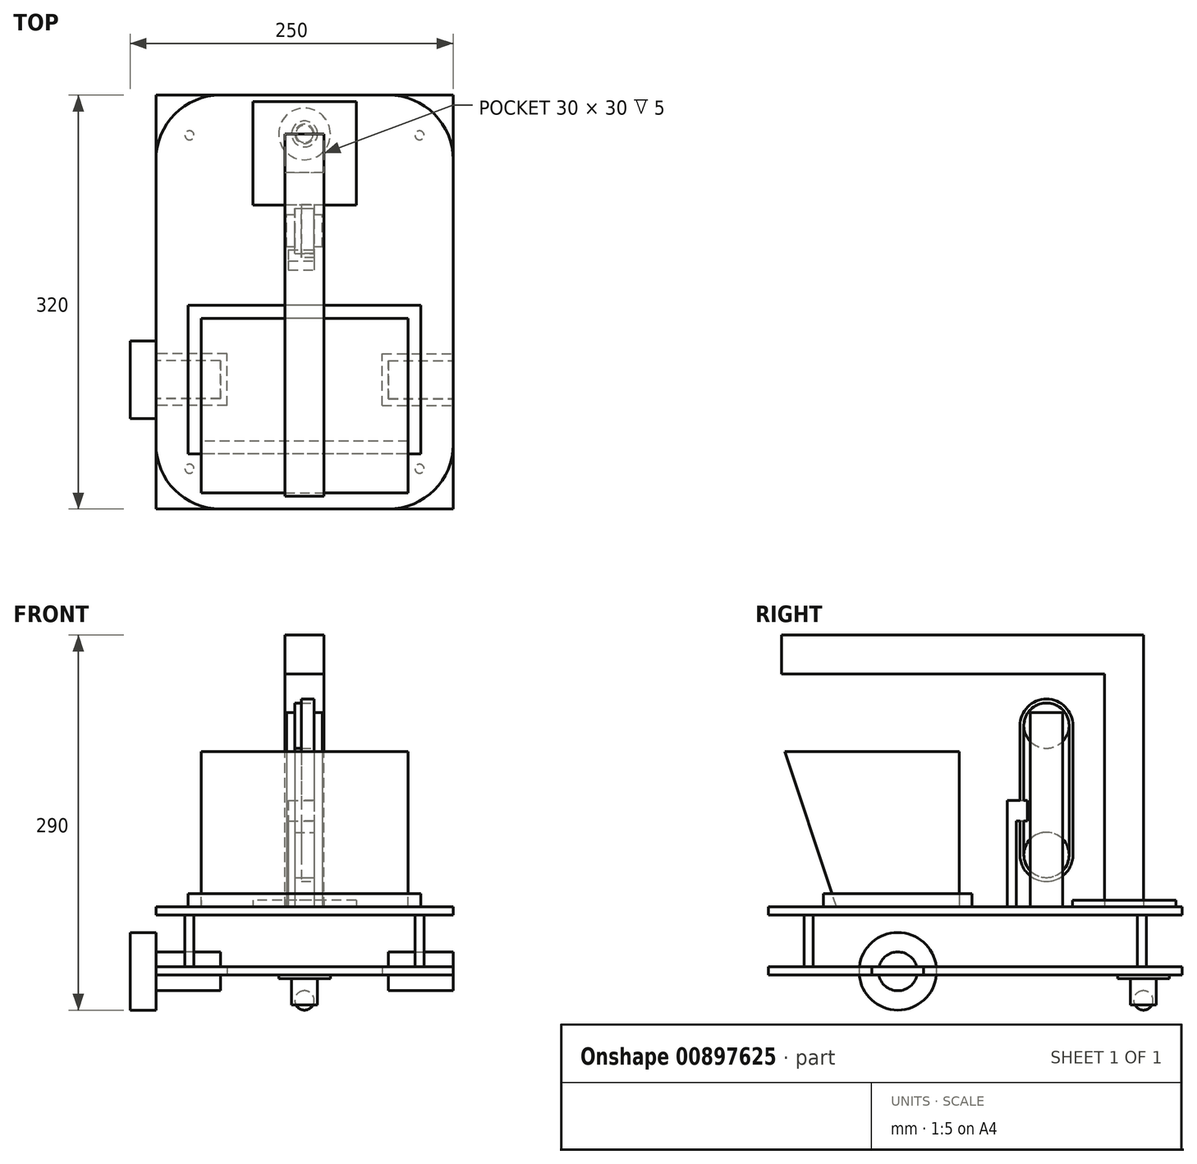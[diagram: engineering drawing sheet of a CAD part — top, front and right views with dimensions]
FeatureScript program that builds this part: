
annotation { "Feature Type Name" : "Feature", "Feature Type Description" : "" }
export const myFeature = defineFeature(function(context is Context, id is Id, definition is map)
    precondition{}
    {
        {
            var Q0;
            Q0=qCreatedBy(makeId("Top.planeOp"),FACE);
            var sketch = newSketch(context, id + "F0", { "sketchPlane" : qUnion([Q0])});
            skLineSegment(sketch, "E0.bottom", {"start": v(0, 0) * mm, "end": v(230, 0) * mm});
            skLineSegment(sketch, "E0.top", {"start": v(0, 320) * mm, "end": v(230, 320) * mm});
            skLineSegment(sketch, "E0.left", {"start": v(0, 0) * mm, "end": v(0, 320) * mm});
            skLineSegment(sketch, "E0.right", {"start": v(230, 0) * mm, "end": v(230, 320) * mm});
            skLineSegment(sketch, "E1.bottom", {"start": v(-20, 130) * mm, "end": v(0, 130) * mm});
            skLineSegment(sketch, "E1.top", {"start": v(-20, 70) * mm, "end": v(0, 70) * mm});
            skLineSegment(sketch, "E1.left", {"start": v(-20, 130) * mm, "end": v(-20, 70) * mm});
            skLineSegment(sketch, "E1.right", {"start": v(0, 130) * mm, "end": v(0, 70) * mm});
            skLineSegment(sketch, "E2.bottom", {"start": v(230, 130) * mm, "end": v(250, 130) * mm});
            skLineSegment(sketch, "E2.top", {"start": v(230, 70) * mm, "end": v(250, 70) * mm});
            skLineSegment(sketch, "E2.left", {"start": v(230, 130) * mm, "end": v(230, 70) * mm});
            skLineSegment(sketch, "E2.right", {"start": v(250, 130) * mm, "end": v(250, 70) * mm});
            skLineSegment(sketch, "E3", {"start": v(-20, 100) * mm, "end": v(250, 100) * mm, "construction": true});
            skSolve(sketch);
        }
        {
            var Q0;
            Q0=qCreatedBy(makeId("Right.planeOp"),FACE);
            var sketch = newSketch(context, id + "F1", { "sketchPlane" : qUnion([Q0])});
            skLineSegment(sketch, "E4.bottom", {"start": v(0, 0) * mm, "end": v(320, 0) * mm});
            skLineSegment(sketch, "E4.top", {"start": v(0, -6.35) * mm, "end": v(320, -6.35) * mm});
            skLineSegment(sketch, "E4.left", {"start": v(0, 0) * mm, "end": v(0, -6.35) * mm});
            skLineSegment(sketch, "E4.right", {"start": v(320, 0) * mm, "end": v(320, -6.35) * mm});
            skLineSegment(sketch, "E5", {"start": v(160, 0) * mm, "end": v(160, -52.7) * mm, "construction": true});
            skLineSegment(sketch, "E6.bottom", {"start": v(0, -52.7) * mm, "end": v(320, -52.7) * mm});
            skLineSegment(sketch, "E6.top", {"start": v(0, -46.35) * mm, "end": v(320, -46.35) * mm});
            skLineSegment(sketch, "E6.left", {"start": v(0, -52.7) * mm, "end": v(0, -46.35) * mm});
            skLineSegment(sketch, "E6.right", {"start": v(320, -52.7) * mm, "end": v(320, -46.35) * mm});
            skPoint(sketch, "E7.0", {"position": v(100, 0) * mm});
            skLineSegment(sketch, "E8", {"start": v(100, 0) * mm, "end": v(100, -50) * mm, "construction": true});
            skPoint(sketch, "E9.0", {"position": v(70, 0) * mm});
            skPoint(sketch, "E10.0", {"position": v(130, 0) * mm});
            skLineSegment(sketch, "E11", {"start": v(70, 0) * mm, "end": v(70, -50) * mm, "construction": true});
            skLineSegment(sketch, "E12", {"start": v(70, -50) * mm, "end": v(100, -50) * mm, "construction": true});
            skCircle(sketch, "E13", {"center": v(100, -50) * mm, "radius": 30 * mm});
            skLineSegment(sketch, "E14", {"start": v(100, -50) * mm, "end": v(100, -80) * mm, "construction": true});
            skSolve(sketch);
        }
        {
            var Q0;
            {var subQ3=sQuery(id+"F0.wireOp",EDGE,"E0.bottom");Q0=makeQuery(id+"F0.imprint","IMPRINT",FACE,{"disambiguationData":[TD([[makeQuery(id+"F0.imprint","IMPRINT",EDGE,{"derivedFrom":subQ3}),1.0]])]});}
            var Q1;
            Q1=sQuery(id+"F1.wireOp",VERTEX,"E4.top.end");
            extrude(context, id + "F2", {"entities" : qUnion([Q0]), "endBound" : BoundingType.UP_TO_VERTEX, "oppositeDirection" : true, "depth" : 25 * mm, "endBoundEntityVertex" : qUnion([Q1]), "offsetDistance" : 25 * mm});
        }
        {
            var Q0;
            {var subQ3=sQuery(id+"F0.wireOp",EDGE,"E0.bottom");Q0=makeQuery(id+"F0.imprint","IMPRINT",FACE,{"disambiguationData":[TD([[makeQuery(id+"F0.imprint","IMPRINT",EDGE,{"derivedFrom":subQ3}),1.0]])]});}
            var Q1;
            Q1=sQuery(id+"F1.wireOp",VERTEX,"E6.bottom.start");
            var Q2;
            Q2=sQuery(id+"F1.wireOp",VERTEX,"E6.top.start");
            extrude(context, id + "F3", {"entities" : qUnion([Q0]), "endBound" : BoundingType.UP_TO_VERTEX, "oppositeDirection" : true, "depth" : 25 * mm, "endBoundEntityVertex" : qUnion([Q1]), "offsetDistance" : 25 * mm, "hasSecondDirection" : true, "secondDirectionBound" : BoundingType.UP_TO_VERTEX, "secondDirectionOppositeDirection" : true, "secondDirectionDepth" : 25 * mm, "secondDirectionBoundEntityVertex" : qUnion([Q2])});
        }
        {
            var Q0;
            Q0=makeQuery(id+"F2.opExtrude","SWEPT_EDGE",EDGE,{"disambiguationData":[OSD([sQuery(id+"F0.wireOp",EDGE,"E0.bottom"),sQuery(id+"F0.wireOp",EDGE,"E0.right")])]});
            var Q1;
            Q1=makeQuery(id+"F2.opExtrude","SWEPT_EDGE",EDGE,{"disambiguationData":[OSD([sQuery(id+"F0.wireOp",EDGE,"E0.top"),sQuery(id+"F0.wireOp",EDGE,"E0.right")])]});
            var Q2;
            Q2=makeQuery(id+"F2.opExtrude","SWEPT_EDGE",EDGE,{"disambiguationData":[OSD([sQuery(id+"F0.wireOp",EDGE,"E0.top"),sQuery(id+"F0.wireOp",EDGE,"E0.left")])]});
            var Q3;
            Q3=makeQuery(id+"F2.opExtrude","SWEPT_EDGE",EDGE,{"disambiguationData":[OSD([sQuery(id+"F0.wireOp",EDGE,"E0.bottom"),sQuery(id+"F0.wireOp",EDGE,"E0.left")])]});
            var Q4;
            {var subQ0=sQuery(id+"F0.wireOp",EDGE,"E2.left");var subQ1=sQuery(id+"F0.wireOp",EDGE,"E0.right");var subQ2=sQuery(id+"F0.wireOp",EDGE,"E0.bottom");Q4=makeQuery(id+"F3.opExtrude","TWEAK_EDGE",EDGE,{"derivedFrom":[makeQuery(id+"F0.imprint","IMPRINT",EDGE,{"derivedFrom":subQ2}),makeQuery(id+"F0.imprint","IMPRINT",EDGE,{"disambiguationData":[TD([[makeQuery(id+"F0.imprint","INTERSECT",VERTEX,{"derivedFrom":[subQ2,subQ1]}),-1.0]])],"derivedFrom":subQ1}),makeQuery(id+"F0.imprint","IMPRINT",EDGE,{"disambiguationData":[TD([[makeQuery(id+"F0.imprint","INTERSECT",VERTEX,{"derivedFrom":[sQuery(id+"F0.wireOp",EDGE,"E0.top"),subQ1]}),1.0]])],"derivedFrom":subQ1}),makeQuery(id+"F0.imprint","IMPRINT",EDGE,{"derivedFrom":subQ0})]});}
            var Q5;
            {var subQ0=sQuery(id+"F0.wireOp",EDGE,"E2.left");var subQ1=sQuery(id+"F0.wireOp",EDGE,"E0.right");var subQ2=sQuery(id+"F0.wireOp",EDGE,"E0.top");Q5=makeQuery(id+"F3.opExtrude","TWEAK_EDGE",EDGE,{"derivedFrom":[makeQuery(id+"F0.imprint","IMPRINT",EDGE,{"derivedFrom":subQ2}),makeQuery(id+"F0.imprint","IMPRINT",EDGE,{"disambiguationData":[TD([[makeQuery(id+"F0.imprint","INTERSECT",VERTEX,{"derivedFrom":[sQuery(id+"F0.wireOp",EDGE,"E0.bottom"),subQ1]}),-1.0]])],"derivedFrom":subQ1}),makeQuery(id+"F0.imprint","IMPRINT",EDGE,{"disambiguationData":[TD([[makeQuery(id+"F0.imprint","INTERSECT",VERTEX,{"derivedFrom":[subQ2,subQ1]}),1.0]])],"derivedFrom":subQ1}),makeQuery(id+"F0.imprint","IMPRINT",EDGE,{"derivedFrom":subQ0})]});}
            var Q6;
            {var subQ0=sQuery(id+"F0.wireOp",EDGE,"E1.right");var subQ1=sQuery(id+"F0.wireOp",EDGE,"E0.left");var subQ2=sQuery(id+"F0.wireOp",EDGE,"E0.top");Q6=makeQuery(id+"F3.opExtrude","TWEAK_EDGE",EDGE,{"derivedFrom":[makeQuery(id+"F0.imprint","IMPRINT",EDGE,{"derivedFrom":subQ2}),makeQuery(id+"F0.imprint","IMPRINT",EDGE,{"disambiguationData":[TD([[makeQuery(id+"F0.imprint","INTERSECT",VERTEX,{"derivedFrom":[sQuery(id+"F0.wireOp",EDGE,"E0.bottom"),subQ1]}),-1.0]])],"derivedFrom":subQ1}),makeQuery(id+"F0.imprint","IMPRINT",EDGE,{"disambiguationData":[TD([[makeQuery(id+"F0.imprint","INTERSECT",VERTEX,{"derivedFrom":[subQ2,subQ1]}),1.0]])],"derivedFrom":subQ1}),makeQuery(id+"F0.imprint","IMPRINT",EDGE,{"derivedFrom":subQ0})]});}
            var Q7;
            {var subQ0=sQuery(id+"F0.wireOp",EDGE,"E1.right");var subQ1=sQuery(id+"F0.wireOp",EDGE,"E0.left");var subQ2=sQuery(id+"F0.wireOp",EDGE,"E0.bottom");Q7=makeQuery(id+"F3.opExtrude","TWEAK_EDGE",EDGE,{"derivedFrom":[makeQuery(id+"F0.imprint","IMPRINT",EDGE,{"derivedFrom":subQ2}),makeQuery(id+"F0.imprint","IMPRINT",EDGE,{"disambiguationData":[TD([[makeQuery(id+"F0.imprint","INTERSECT",VERTEX,{"derivedFrom":[subQ2,subQ1]}),-1.0]])],"derivedFrom":subQ1}),makeQuery(id+"F0.imprint","IMPRINT",EDGE,{"disambiguationData":[TD([[makeQuery(id+"F0.imprint","INTERSECT",VERTEX,{"derivedFrom":[sQuery(id+"F0.wireOp",EDGE,"E0.top"),subQ1]}),1.0]])],"derivedFrom":subQ1}),makeQuery(id+"F0.imprint","IMPRINT",EDGE,{"derivedFrom":subQ0})]});}
            fillet(context, id + "F4", {"entities" : qUnion([Q0, Q1, Q2, Q3, Q4, Q5, Q6, Q7]), "radius" : 50 * mm, "tangentPropagation" : true, "allowEdgeOverflow" : false});
        }
        {
            var Q0;
            Q0=makeQuery(id+"F2.opExtrude","SWEPT_FACE",FACE,{"disambiguationData":[OSD([sQuery(id+"F0.wireOp",EDGE,"E0.left"),sQuery(id+"F0.wireOp",EDGE,"E1.right")])]});
            var Q1;
            Q1=makeQuery(id+"F2.opExtrude","SWEPT_FACE",FACE,{"disambiguationData":[OSD([sQuery(id+"F0.wireOp",EDGE,"E0.right"),sQuery(id+"F0.wireOp",EDGE,"E2.left")])]});
            cPlane(context, id + "F5", {"entities" : qUnion([Q0, Q1]), "cplaneType" : CPlaneType.MID_PLANE, "offset" : 25 * mm, "width" : 150 * mm, "height" : 150 * mm});
        }
        {
            var Q0;
            {var subQ0=sQuery(id+"F1.wireOp",EDGE,"E13");var subQ1=sQuery(id+"F1.wireOp",EDGE,"E6.bottom");var subQ2=makeQuery(id+"F1.imprint","INTERSECT",VERTEX,{"disambiguationData":[OD(0.0)],"derivedFrom":[subQ1,subQ0]});Q0=makeQuery(id+"F1.imprint","IMPRINT",FACE,{"disambiguationData":[TD([[makeQuery(id+"F1.imprint","IMPRINT",EDGE,{"disambiguationData":[TD([[subQ2,-1.0]])],"derivedFrom":subQ1}),1.0]])]});}
            var Q1;
            {var subQ0=sQuery(id+"F1.wireOp",EDGE,"E13");var subQ1=sQuery(id+"F1.wireOp",EDGE,"E6.bottom");var subQ2=makeQuery(id+"F1.imprint","INTERSECT",VERTEX,{"disambiguationData":[OD(0.0)],"derivedFrom":[subQ1,subQ0]});Q1=makeQuery(id+"F1.imprint","IMPRINT",FACE,{"disambiguationData":[TD([[makeQuery(id+"F1.imprint","IMPRINT",EDGE,{"disambiguationData":[TD([[subQ2,-1.0]])],"derivedFrom":subQ1}),-1.0]])]});}
            var Q2;
            {var subQ0=sQuery(id+"F1.wireOp",EDGE,"E13");var subQ1=sQuery(id+"F1.wireOp",EDGE,"E6.top");var subQ2=makeQuery(id+"F1.imprint","INTERSECT",VERTEX,{"disambiguationData":[OD(0.0)],"derivedFrom":[subQ1,subQ0]});Q2=makeQuery(id+"F1.imprint","IMPRINT",FACE,{"disambiguationData":[TD([[makeQuery(id+"F1.imprint","IMPRINT",EDGE,{"disambiguationData":[TD([[subQ2,-1.0]])],"derivedFrom":subQ1}),1.0]])]});}
            var Q3;
            Q3=sQuery(id+"F0.wireOp",VERTEX,"E3.start");
            extrude(context, id + "F6", {"entities" : qUnion([Q0, Q1, Q2]), "operationType" : NewBodyOperationType.ADD, "endBound" : BoundingType.UP_TO_VERTEX, "oppositeDirection" : true, "depth" : 25 * mm, "endBoundEntityVertex" : qUnion([Q3]), "offsetDistance" : 25 * mm});
        }
        {
            var Q0;
            Q0=makeQuery(id+"F6.opExtrude","CAP_FACE",FACE,{"disambiguationData":[OSD([sQuery(id+"F1.wireOp",EDGE,"E13")])],"isStart":true});
            var sketch = newSketch(context, id + "F7", { "sketchPlane" : qUnion([Q0])});
            skPoint(sketch, "E15.0", {"position": v(100, -50) * mm});
            skCircle(sketch, "E16", {"center": v(100, -50) * mm, "radius": 15 * mm});
            skSolve(sketch);
        }
        {
            var Q0;
            Q0 = qSketchRegion(id + "F7", true);
            extrude(context, id + "F8", {"entities" : qUnion([Q0]), "depth" : 50 * mm, "offsetDistance" : 25 * mm});
        }
        {
            var Q0;
            Q0=makeQuery(id+"F3.opExtrude","CAP_FACE",FACE,{"disambiguationData":[OSD([sQuery(id+"F0.wireOp",EDGE,"E0.bottom"),sQuery(id+"F0.wireOp",EDGE,"E0.top"),sQuery(id+"F0.wireOp",EDGE,"E0.left"),sQuery(id+"F0.wireOp",EDGE,"E0.right"),sQuery(id+"F0.wireOp",EDGE,"E1.right"),sQuery(id+"F0.wireOp",EDGE,"E2.left")])],"isStart":true});
            var sketch = newSketch(context, id + "F9", { "sketchPlane" : qUnion([Q0])});
            skLineSegment(sketch, "E17.0", {"start": v(0, 50) * mm, "end": v(0, 270) * mm, "construction": true});
            skArc(sketch, "E17.1", {"start": v(50, 320) * mm, "mid": v(14.64, 305.36) * mm, "end": v(0, 270) * mm, "construction": true});
            skLineSegment(sketch, "E17.2", {"start": v(50, 320) * mm, "end": v(180, 320) * mm, "construction": true});
            skArc(sketch, "E17.3", {"start": v(230, 270) * mm, "mid": v(215.36, 305.36) * mm, "end": v(180, 320) * mm, "construction": true});
            skLineSegment(sketch, "E17.4", {"start": v(230, 270) * mm, "end": v(230, 50) * mm, "construction": true});
            skArc(sketch, "E17.5", {"start": v(180, 0) * mm, "mid": v(215.36, 14.64) * mm, "end": v(230, 50) * mm, "construction": true});
            skLineSegment(sketch, "E17.6", {"start": v(50, 0) * mm, "end": v(180, 0) * mm, "construction": true});
            skArc(sketch, "E17.7", {"start": v(0, 50) * mm, "mid": v(14.64, 14.64) * mm, "end": v(50, 0) * mm, "construction": true});
            skLineSegment(sketch, "E18", {"start": v(14.64, 305.36) * mm, "end": v(215.36, 14.64) * mm, "construction": true});
            skLineSegment(sketch, "E19", {"start": v(215.36, 305.36) * mm, "end": v(14.64, 14.64) * mm, "construction": true});
            skLineSegment(sketch, "E20", {"start": v(115, 320) * mm, "end": v(115, 0) * mm, "construction": true});
            skCircle(sketch, "E21", {"center": v(26, 288.9) * mm, "radius": 3.5 * mm});
            skCircle(sketch, "E22", {"center": v(26, 31.1) * mm, "radius": 3.5 * mm});
            skLineSegment(sketch, "E23", {"start": v(14.64, 305.36) * mm, "end": v(26, 288.9) * mm, "construction": true});
            skLineSegment(sketch, "E24", {"start": v(26, 31.1) * mm, "end": v(14.64, 14.64) * mm, "construction": true});
            skSolve(sketch);
        }
        {
            var Q0;
            Q0=makeQuery(id+"F9.imprint","IMPRINT",FACE,{"disambiguationData":[TD([[makeQuery(id+"F9.imprint","IMPRINT",EDGE,{"derivedFrom":sQuery(id+"F9.wireOp",EDGE,"E21")}),1.0]])]});
            var Q1;
            Q1=makeQuery(id+"F9.imprint","IMPRINT",FACE,{"disambiguationData":[TD([[makeQuery(id+"F9.imprint","IMPRINT",EDGE,{"derivedFrom":sQuery(id+"F9.wireOp",EDGE,"E22")}),1.0]])]});
            var Q2;
            Q2=makeQuery(id+"F2.opExtrude","CAP_FACE",FACE,{"disambiguationData":[OSD([sQuery(id+"F0.wireOp",EDGE,"E0.bottom"),sQuery(id+"F0.wireOp",EDGE,"E0.top"),sQuery(id+"F0.wireOp",EDGE,"E0.left"),sQuery(id+"F0.wireOp",EDGE,"E0.right"),sQuery(id+"F0.wireOp",EDGE,"E1.right"),sQuery(id+"F0.wireOp",EDGE,"E2.left")])],"isStart":false});
            extrude(context, id + "F10", {"entities" : qUnion([Q0, Q1]), "endBound" : BoundingType.UP_TO_SURFACE, "depth" : 25 * mm, "endBoundEntityFace" : qUnion([Q2]), "offsetDistance" : 25 * mm});
        }
        {
            var Q0;
            Q0=makeQuery(id+"F2.opExtrude","CAP_FACE",FACE,{"disambiguationData":[OSD([sQuery(id+"F0.wireOp",EDGE,"E0.bottom"),sQuery(id+"F0.wireOp",EDGE,"E0.top"),sQuery(id+"F0.wireOp",EDGE,"E0.left"),sQuery(id+"F0.wireOp",EDGE,"E0.right"),sQuery(id+"F0.wireOp",EDGE,"E1.right"),sQuery(id+"F0.wireOp",EDGE,"E2.left")])],"isStart":true});
            var sketch = newSketch(context, id + "F11", { "sketchPlane" : qUnion([Q0])});
            skLineSegment(sketch, "E25", {"start": v(115, 320) * mm, "end": v(115, 0) * mm, "construction": true});
            skLineSegment(sketch, "E26.bottom", {"start": v(195, 147.5) * mm, "end": v(35, 147.5) * mm});
            skLineSegment(sketch, "E26.top", {"start": v(195, 52.5) * mm, "end": v(35, 52.5) * mm});
            skLineSegment(sketch, "E26.left", {"start": v(195, 147.5) * mm, "end": v(195, 52.5) * mm});
            skLineSegment(sketch, "E26.right", {"start": v(35, 147.5) * mm, "end": v(35, 52.5) * mm});
            skPoint(sketch, "E26.middle", {"position": v(115, 100) * mm});
            skLineSegment(sketch, "E27.bottom", {"start": v(155, 315) * mm, "end": v(75, 315) * mm});
            skLineSegment(sketch, "E27.top", {"start": v(155, 235) * mm, "end": v(75, 235) * mm});
            skLineSegment(sketch, "E27.left", {"start": v(155, 315) * mm, "end": v(155, 235) * mm});
            skLineSegment(sketch, "E27.right", {"start": v(75, 315) * mm, "end": v(75, 235) * mm});
            skPoint(sketch, "E27.middle", {"position": v(115, 275) * mm});
            skLineSegment(sketch, "E28.bottom", {"start": v(130, 290) * mm, "end": v(100, 290) * mm});
            skLineSegment(sketch, "E28.top", {"start": v(130, 260) * mm, "end": v(100, 260) * mm});
            skLineSegment(sketch, "E28.left", {"start": v(130, 290) * mm, "end": v(130, 260) * mm});
            skLineSegment(sketch, "E28.right", {"start": v(100, 290) * mm, "end": v(100, 260) * mm});
            skLineSegment(sketch, "E29.0", {"start": v(205, 157.5) * mm, "end": v(25, 157.5) * mm});
            skLineSegment(sketch, "E29.1", {"start": v(205, 157.5) * mm, "end": v(205, 42.5) * mm});
            skLineSegment(sketch, "E29.2", {"start": v(205, 42.5) * mm, "end": v(25, 42.5) * mm});
            skLineSegment(sketch, "E29.3", {"start": v(25, 157.5) * mm, "end": v(25, 42.5) * mm});
            skPoint(sketch, "E30.middle", {"position": v(115, 215) * mm});
            skLineSegment(sketch, "E31", {"start": v(125.67, 215) * mm, "end": v(104.32, 215) * mm, "construction": true});
            skLineSegment(sketch, "E32.bottom", {"start": v(128.85, 202.5) * mm, "end": v(122.5, 202.5) * mm});
            skLineSegment(sketch, "E32.top", {"start": v(128.85, 227.5) * mm, "end": v(122.5, 227.5) * mm});
            skLineSegment(sketch, "E32.left", {"start": v(128.85, 202.5) * mm, "end": v(128.85, 227.5) * mm});
            skLineSegment(sketch, "E32.right", {"start": v(122.5, 202.5) * mm, "end": v(122.5, 227.5) * mm});
            skPoint(sketch, "E32.middle", {"position": v(125.67, 215) * mm});
            skLineSegment(sketch, "E33.bottom", {"start": v(107.5, 202.5) * mm, "end": v(101.15, 202.5) * mm});
            skLineSegment(sketch, "E33.top", {"start": v(107.5, 227.5) * mm, "end": v(101.15, 227.5) * mm});
            skLineSegment(sketch, "E33.left", {"start": v(107.5, 202.5) * mm, "end": v(107.5, 227.5) * mm});
            skLineSegment(sketch, "E33.right", {"start": v(101.15, 202.5) * mm, "end": v(101.15, 227.5) * mm});
            skPoint(sketch, "E33.middle", {"position": v(104.32, 215) * mm});
            skPoint(sketch, "E34", {"position": v(115, 157.5) * mm});
            skSolve(sketch);
        }
        {
            var Q0;
            Q0=makeQuery(id+"F11.imprint","IMPRINT",FACE,{"disambiguationData":[TD([[makeQuery(id+"F11.imprint","IMPRINT",EDGE,{"derivedFrom":sQuery(id+"F11.wireOp",EDGE,"E26.bottom")}),1.0]])]});
            extrude(context, id + "F12", {"entities" : qUnion([Q0]), "operationType" : NewBodyOperationType.ADD, "depth" : 120 * mm, "offsetDistance" : 25 * mm});
        }
        {
            var Q0;
            Q0=makeQuery(id+"F11.imprint","IMPRINT",FACE,{"disambiguationData":[TD([[makeQuery(id+"F11.imprint","IMPRINT",EDGE,{"derivedFrom":sQuery(id+"F11.wireOp",EDGE,"E27.bottom")}),1.0]])]});
            extrude(context, id + "F13", {"entities" : qUnion([Q0]), "operationType" : NewBodyOperationType.ADD, "depth" : 5 * mm, "offsetDistance" : 25 * mm});
        }
        {
            var Q0;
            Q0=makeQuery(id+"F12.opExtrude","SWEPT_FACE",FACE,{"disambiguationData":[OSD([sQuery(id+"F11.wireOp",EDGE,"E26.left")])]});
            var sketch = newSketch(context, id + "F14", { "sketchPlane" : qUnion([Q0])});
            skLineSegment(sketch, "E35", {"start": v(52.5, 0) * mm, "end": v(12.5, 120) * mm});
            skLineSegment(sketch, "E36", {"start": v(12.5, 120) * mm, "end": v(52.5, 120) * mm});
            skLineSegment(sketch, "E37.0", {"start": v(52.5, 120) * mm, "end": v(52.5, 0) * mm});
            skSolve(sketch);
        }
        {
            var Q0;
            Q0=makeQuery(id+"F14.imprint","IMPRINT",FACE,{"disambiguationData":[TD([[makeQuery(id+"F14.imprint","IMPRINT",EDGE,{"derivedFrom":sQuery(id+"F14.wireOp",EDGE,"E35")}),-1.0]])]});
            var Q1;
            Q1=makeQuery(id+"F12.opExtrude","SWEPT_FACE",FACE,{"disambiguationData":[OSD([sQuery(id+"F11.wireOp",EDGE,"E26.right")])]});
            var Q2;
            Q2=makeQuery(id+"F12.opExtrude","CAP_VERTEX",VERTEX,{"disambiguationData":[OSD([sQuery(id+"F11.wireOp",EDGE,"E26.top"),sQuery(id+"F11.wireOp",EDGE,"E26.right")])],"isStart":false});
            extrude(context, id + "F15", {"entities" : qUnion([Q0]), "operationType" : NewBodyOperationType.ADD, "endBound" : BoundingType.UP_TO_VERTEX, "oppositeDirection" : true, "depth" : 25 * mm, "endBoundEntityFace" : qUnion([Q1]), "endBoundEntityVertex" : qUnion([Q2]), "offsetDistance" : 25 * mm});
        }
        {
            var Q0;
            Q0=makeQuery(id+"F12.opExtrude","CAP_FACE",FACE,{"disambiguationData":[OSD([sQuery(id+"F11.wireOp",EDGE,"E26.bottom"),sQuery(id+"F11.wireOp",EDGE,"E26.top"),sQuery(id+"F11.wireOp",EDGE,"E26.left"),sQuery(id+"F11.wireOp",EDGE,"E26.right")])],"isStart":false});
            shell(context, id + "F16", {"entities" : qUnion([Q0]), "thickness" : 0.05 * mm});
        }
        {
            var Q0;
            Q0=makeQuery(id+"F3.opExtrude","CAP_FACE",FACE,{"disambiguationData":[OSD([sQuery(id+"F0.wireOp",EDGE,"E0.bottom"),sQuery(id+"F0.wireOp",EDGE,"E0.top"),sQuery(id+"F0.wireOp",EDGE,"E0.left"),sQuery(id+"F0.wireOp",EDGE,"E0.right"),sQuery(id+"F0.wireOp",EDGE,"E1.right"),sQuery(id+"F0.wireOp",EDGE,"E2.left")])],"isStart":false});
            var sketch = newSketch(context, id + "F17", { "sketchPlane" : qUnion([Q0])});
            skLineSegment(sketch, "E38.0", {"start": v(0, -85) * mm, "end": v(0, -115) * mm});
            skLineSegment(sketch, "E39.0", {"start": v(50, -85) * mm, "end": v(50, -115) * mm, "construction": true});
            skLineSegment(sketch, "E40", {"start": v(50, -115) * mm, "end": v(0, -115) * mm, "construction": true});
            skLineSegment(sketch, "E41", {"start": v(50, -85) * mm, "end": v(0, -85) * mm, "construction": true});
            skLineSegment(sketch, "E42.0", {"start": v(55, -120) * mm, "end": v(0, -120) * mm});
            skLineSegment(sketch, "E42.1", {"start": v(55, -80) * mm, "end": v(55, -120) * mm});
            skLineSegment(sketch, "E42.2", {"start": v(55, -80) * mm, "end": v(0, -80) * mm});
            skLineSegment(sketch, "E43", {"start": v(115, -320) * mm, "end": v(115, -290) * mm, "construction": true});
            skCircle(sketch, "E44", {"center": v(115, -290) * mm, "radius": 20 * mm});
            skLineSegment(sketch, "E45.MirrorCS", {"start": v(175, -120) * mm, "end": v(230, -120) * mm});
            skLineSegment(sketch, "E46.MirrorCS", {"start": v(175, -80) * mm, "end": v(230, -80) * mm});
            skLineSegment(sketch, "E47.MirrorCS", {"start": v(175, -80) * mm, "end": v(175, -120) * mm});
            skSolve(sketch);
        }
        {
            var Q0;
            {var subQ1=sQuery(id+"F17.wireOp",EDGE,"E38.0");Q0=makeQuery(id+"F17.imprint","IMPRINT",FACE,{"disambiguationData":[TD([[makeQuery(id+"F17.imprint","IMPRINT",EDGE,{"derivedFrom":subQ1}),1.0]])]});}
            var Q1;
            {var subQ0=sQuery(id+"F17.wireOp",EDGE,"E45.MirrorCS");Q1=makeQuery(id+"F17.imprint","IMPRINT",FACE,{"disambiguationData":[TD([[makeQuery(id+"F17.imprint","IMPRINT",EDGE,{"derivedFrom":subQ0}),1.0]])]});}
            var Q2;
            Q2=makeQuery(id+"F3.opExtrude","CAP_FACE",FACE,{"disambiguationData":[OSD([sQuery(id+"F0.wireOp",EDGE,"E0.bottom"),sQuery(id+"F0.wireOp",EDGE,"E0.top"),sQuery(id+"F0.wireOp",EDGE,"E0.left"),sQuery(id+"F0.wireOp",EDGE,"E0.right"),sQuery(id+"F0.wireOp",EDGE,"E1.right"),sQuery(id+"F0.wireOp",EDGE,"E2.left")])],"isStart":true});
            extrude(context, id + "F18", {"entities" : qUnion([Q0, Q1]), "operationType" : NewBodyOperationType.REMOVE, "endBound" : BoundingType.UP_TO_SURFACE, "oppositeDirection" : true, "depth" : 25 * mm, "endBoundEntityFace" : qUnion([Q2]), "offsetDistance" : 25 * mm});
        }
        {
            var Q0;
            Q0=qCreatedBy(makeId("Front.planeOp"),FACE);
            var Q1;
            Q1=sQuery(id+"F17.wireOp",VERTEX,"E43.end");
            cPlane(context, id + "F19", {"entities" : qUnion([Q0, Q1]), "cplaneType" : CPlaneType.PLANE_POINT, "offset" : 25 * mm, "width" : 150 * mm, "height" : 150 * mm});
        }
        {
            var Q0;
            Q0=qCreatedBy(id+"F19.planeOp",FACE);
            var sketch = newSketch(context, id + "F20", { "sketchPlane" : qUnion([Q0])});
            skPoint(sketch, "E48.0", {"position": v(115, -52.7) * mm});
            skLineSegment(sketch, "E49.0", {"start": v(115, -52.7) * mm, "end": v(95, -52.7) * mm});
            skLineSegment(sketch, "E50", {"start": v(115, -52.7) * mm, "end": v(115, -76) * mm});
            skLineSegment(sketch, "E51", {"start": v(115, -76) * mm, "end": v(105, -76) * mm});
            skLineSegment(sketch, "E52", {"start": v(95, -55.7) * mm, "end": v(95, -52.7) * mm});
            skArc(sketch, "E53", {"start": v(115, -65) * mm, "mid": v(107.5, -72.5) * mm, "end": v(115, -80) * mm});
            skLineSegment(sketch, "E54", {"start": v(105, -76) * mm, "end": v(105, -55.7) * mm});
            skLineSegment(sketch, "E55", {"start": v(105, -55.7) * mm, "end": v(95, -55.7) * mm});
            skLineSegment(sketch, "E56", {"start": v(115, -80) * mm, "end": v(115, -76) * mm});
            skLineSegment(sketch, "E57.0", {"start": v(0, -20) * mm, "end": v(0, -80) * mm});
            skLineSegment(sketch, "E58", {"start": v(0, -80) * mm, "end": v(115, -80) * mm, "construction": true});
            skSolve(sketch);
        }
        {
            var Q0;
            {var subQ0=sQuery(id+"F20.wireOp",EDGE,"E56");Q0=makeQuery(id+"F20.imprint","IMPRINT",FACE,{"disambiguationData":[TD([[makeQuery(id+"F20.imprint","IMPRINT",EDGE,{"derivedFrom":subQ0}),1.0]])]});}
            var Q1;
            {var subQ5=sQuery(id+"F20.wireOp",EDGE,"E49.0");Q1=makeQuery(id+"F20.imprint","IMPRINT",FACE,{"disambiguationData":[TD([[makeQuery(id+"F20.imprint","IMPRINT",EDGE,{"derivedFrom":subQ5}),1.0]])]});}
            var Q2;
            Q2=sQuery(id+"F20.wireOp",EDGE,"E50");
            revolve(context, id + "F21", {"surfaceOperationType" : NewSurfaceOperationType.NEW, "entities" : qUnion([Q0, Q1]), "axis" : qUnion([Q2]), "revolveType" : RevolveType.FULL});
        }
        {
            var Q0;
            Q0=qCreatedBy(makeId("Right.planeOp"),FACE);
            var Q1;
            Q1=sQuery(id+"F11.wireOp",VERTEX,"E28.bottom.start");
            cPlane(context, id + "F22", {"entities" : qUnion([Q0, Q1]), "cplaneType" : CPlaneType.PLANE_POINT, "offset" : 25 * mm, "width" : 150 * mm, "height" : 150 * mm});
        }
        {
            var Q0;
            Q0=qCreatedBy(id+"F22.planeOp",FACE);
            var sketch = newSketch(context, id + "F23", { "sketchPlane" : qUnion([Q0])});
            skPoint(sketch, "E59.0", {"position": v(290, 0) * mm});
            skPoint(sketch, "E60.0", {"position": v(260, 0) * mm});
            skLineSegment(sketch, "E61.bottom", {"start": v(290, 0) * mm, "end": v(260, 0) * mm});
            skLineSegment(sketch, "E61.top", {"start": v(290, 210) * mm, "end": v(260, 210) * mm});
            skLineSegment(sketch, "E61.left", {"start": v(290, 0) * mm, "end": v(290, 210) * mm});
            skLineSegment(sketch, "E61.right", {"start": v(260, 0) * mm, "end": v(260, 180) * mm});
            skLineSegment(sketch, "E62.bottom", {"start": v(260, 210) * mm, "end": v(10, 210) * mm});
            skLineSegment(sketch, "E62.top", {"start": v(260, 180) * mm, "end": v(10, 180) * mm});
            skLineSegment(sketch, "E62.right", {"start": v(10, 210) * mm, "end": v(10, 180) * mm});
            skSolve(sketch);
        }
        {
            var Q0;
            Q0 = qSketchRegion(id + "F23", true);
            var Q1;
            Q1=sQuery(id+"F11.wireOp",VERTEX,"E28.top.end");
            extrude(context, id + "F24", {"entities" : qUnion([Q0]), "endBound" : BoundingType.UP_TO_VERTEX, "oppositeDirection" : true, "depth" : 25 * mm, "endBoundEntityVertex" : qUnion([Q1]), "offsetDistance" : 25 * mm});
        }
        {
            var Q0;
            Q0=makeQuery(id+"F6.opExtrude","SWEPT_BODY",BODY,{"disambiguationData":[OSD([sQuery(id+"F1.wireOp",EDGE,"E13")])]});
            var Q1;
            Q1=makeQuery(id+"F8.opExtrude","SWEPT_BODY",BODY,{"disambiguationData":[OSD([sQuery(id+"F7.wireOp",EDGE,"E16")])]});
            var Q2;
            Q2=makeQuery(id+"F10.opExtrude","SWEPT_BODY",BODY,{"disambiguationData":[OSD([sQuery(id+"F9.wireOp",EDGE,"E21")])]});
            var Q3;
            Q3=makeQuery(id+"F10.opExtrude","SWEPT_BODY",BODY,{"disambiguationData":[OSD([sQuery(id+"F9.wireOp",EDGE,"E22")])]});
            var Q4;
            Q4=qCreatedBy(id+"F5.planeOp",FACE);
            mirror(context, id + "F25", {"entities" : qUnion([Q0, Q1, Q2, Q3]), "mirrorPlane" : qUnion([Q4])});
        }
        {
            var Q0;
            Q0=makeQuery(id+"F11.imprint","IMPRINT",FACE,{"disambiguationData":[TD([[makeQuery(id+"F11.imprint","IMPRINT",EDGE,{"derivedFrom":sQuery(id+"F11.wireOp",EDGE,"E26.bottom")}),1.0]])]});
            var Q1;
            Q1=makeQuery(id+"F11.imprint","IMPRINT",FACE,{"disambiguationData":[TD([[makeQuery(id+"F11.imprint","IMPRINT",EDGE,{"derivedFrom":sQuery(id+"F11.wireOp",EDGE,"E26.bottom")}),-1.0]])]});
            extrude(context, id + "F26", {"entities" : qUnion([Q0, Q1]), "depth" : 10 * mm, "offsetDistance" : 25 * mm});
        }
        {
            var Q0;
            Q0=makeQuery(id+"F11.imprint","IMPRINT",FACE,{"disambiguationData":[TD([[makeQuery(id+"F11.imprint","IMPRINT",EDGE,{"derivedFrom":sQuery(id+"F11.wireOp",EDGE,"E32.bottom")}),-1.0]])]});
            var Q1;
            Q1=makeQuery(id+"F11.imprint","IMPRINT",FACE,{"disambiguationData":[TD([[makeQuery(id+"F11.imprint","IMPRINT",EDGE,{"derivedFrom":sQuery(id+"F11.wireOp",EDGE,"E33.bottom")}),-1.0]])]});
            extrude(context, id + "F27", {"entities" : qUnion([Q0, Q1]), "depth" : 150 * mm, "offsetDistance" : 25 * mm});
        }
        {
            var Q0;
            Q0=makeQuery(id+"F27.opExtrude","SWEPT_FACE",FACE,{"disambiguationData":[OSD([sQuery(id+"F11.wireOp",EDGE,"E32.right")])]});
            var Q1;
            Q1=makeQuery(id+"F27.opExtrude","SWEPT_FACE",FACE,{"disambiguationData":[OSD([sQuery(id+"F11.wireOp",EDGE,"E32.right")])]});
            var sketch = newSketch(context, id + "F28", { "sketchPlane" : qUnion([Q0, Q1])});
            skPoint(sketch, "E63.0", {"position": v(-215, 150) * mm});
            skPoint(sketch, "E64.0", {"position": v(-215, 0) * mm});
            skLineSegment(sketch, "E65", {"start": v(-215, 150) * mm, "end": v(-215, 140) * mm, "construction": true});
            skCircle(sketch, "E66", {"center": v(-215, 140) * mm, "radius": 17.5 * mm});
            skCircle(sketch, "E67", {"center": v(-215, 40) * mm, "radius": 17.5 * mm});
            skLineSegment(sketch, "E68", {"start": v(-215, 140) * mm, "end": v(-215, 40) * mm, "construction": true});
            skLineSegment(sketch, "E69", {"start": v(-232.5, 140) * mm, "end": v(-232.5, 40) * mm});
            skLineSegment(sketch, "E70", {"start": v(-197.5, 140) * mm, "end": v(-197.5, 40) * mm});
            skLineSegment(sketch, "E71.0", {"start": v(-235.5, 140) * mm, "end": v(-235.5, 40) * mm});
            skLineSegment(sketch, "E72.0", {"start": v(-194.5, 140) * mm, "end": v(-194.5, 40) * mm});
            skArc(sketch, "E73.0", {"start": v(-194.5, 140) * mm, "mid": v(-215, 160.5) * mm, "end": v(-235.5, 140) * mm});
            skArc(sketch, "E74.trimOffspring", {"start": v(-235.5, 40) * mm, "mid": v(-215, 19.5) * mm, "end": v(-194.5, 40) * mm});
            skLineSegment(sketch, "E75.bottom", {"start": v(-200.3, 82.15) * mm, "end": v(-191.7, 82.15) * mm});
            skLineSegment(sketch, "E75.top", {"start": v(-200.3, 66.3) * mm, "end": v(-191.7, 66.3) * mm});
            skLineSegment(sketch, "E75.left", {"start": v(-200.3, 82.15) * mm, "end": v(-200.3, 66.3) * mm});
            skLineSegment(sketch, "E75.right", {"start": v(-191.7, 82.15) * mm, "end": v(-191.7, 66.3) * mm});
            skLineSegment(sketch, "E76", {"start": v(-200.3, 74.22) * mm, "end": v(-197.5, 74.22) * mm, "construction": true});
            skLineSegment(sketch, "E77", {"start": v(-194.5, 74.22) * mm, "end": v(-191.7, 74.22) * mm, "construction": true});
            skPoint(sketch, "E77.startSnap0", {"position": v(-191.7, 74.22) * mm});
            skLineSegment(sketch, "E78.bottom", {"start": v(-191.7, 82.15) * mm, "end": v(-184.74, 82.15) * mm});
            skLineSegment(sketch, "E78.top", {"start": v(-191.7, 0) * mm, "end": v(-184.74, 0) * mm});
            skLineSegment(sketch, "E78.left", {"start": v(-191.7, 82.15) * mm, "end": v(-191.7, 0) * mm});
            skLineSegment(sketch, "E78.right", {"start": v(-184.74, 82.15) * mm, "end": v(-184.74, 0) * mm});
            skSolve(sketch);
        }
        {
            var Q0;
            {var subQ0=sQuery(id+"F28.wireOp",EDGE,"E66");var subQ1=makeQuery(id+"F27.opExtrude","CAP_EDGE",EDGE,{"disambiguationData":[OSD([sQuery(id+"F11.wireOp",EDGE,"E32.right")])],"isStart":false});var subQ2=makeQuery(id+"F28.imprint","INTERSECT",VERTEX,{"disambiguationData":[OD(0.0)],"derivedFrom":[subQ1,subQ0]});Q0=makeQuery(id+"F28.imprint","IMPRINT",FACE,{"disambiguationData":[TD([[makeQuery(id+"F28.imprint","IMPRINT",EDGE,{"disambiguationData":[TD([[subQ2,-1.0]])],"derivedFrom":subQ0}),1.0]])]});}
            var Q1;
            {var subQ0=sQuery(id+"F28.wireOp",EDGE,"E66");var subQ1=makeQuery(id+"F27.opExtrude","SWEPT_EDGE",EDGE,{"disambiguationData":[OSD([sQuery(id+"F11.wireOp",EDGE,"E32.top"),sQuery(id+"F11.wireOp",EDGE,"E32.right")])]});var subQ2=makeQuery(id+"F28.imprint","INTERSECT",VERTEX,{"disambiguationData":[OD(0.0)],"derivedFrom":[subQ1,subQ0]});Q1=makeQuery(id+"F28.imprint","IMPRINT",FACE,{"disambiguationData":[TD([[makeQuery(id+"F28.imprint","IMPRINT",EDGE,{"disambiguationData":[TD([[subQ2,-1.0]])],"derivedFrom":subQ0}),1.0]])]});}
            var Q2;
            {var subQ0=sQuery(id+"F28.wireOp",EDGE,"E66");var subQ1=makeQuery(id+"F27.opExtrude","SWEPT_EDGE",EDGE,{"disambiguationData":[OSD([sQuery(id+"F11.wireOp",EDGE,"E29.0"),sQuery(id+"F11.wireOp",EDGE,"E32.bottom"),sQuery(id+"F11.wireOp",EDGE,"E32.right")])]});var subQ2=makeQuery(id+"F28.imprint","INTERSECT",VERTEX,{"disambiguationData":[OD(0.0)],"derivedFrom":[subQ1,subQ0]});Q2=makeQuery(id+"F28.imprint","IMPRINT",FACE,{"disambiguationData":[TD([[makeQuery(id+"F28.imprint","IMPRINT",EDGE,{"disambiguationData":[TD([[subQ2,1.0]])],"derivedFrom":subQ0}),1.0]])]});}
            var Q3;
            {var subQ0=sQuery(id+"F28.wireOp",EDGE,"E66");var subQ1=sQuery(id+"F11.wireOp",EDGE,"E32.right");var subQ2=makeQuery(id+"F27.opExtrude","CAP_EDGE",EDGE,{"disambiguationData":[OSD([subQ1])],"isStart":false});var subQ3=makeQuery(id+"F28.imprint","INTERSECT",VERTEX,{"disambiguationData":[OD(0.0)],"derivedFrom":[subQ2,subQ0]});Q3=makeQuery(id+"F28.imprint","IMPRINT",FACE,{"disambiguationData":[TD([[makeQuery(id+"F28.imprint","IMPRINT",EDGE,{"disambiguationData":[TD([[subQ3,-1.0]])],"derivedFrom":subQ2}),1.0]])]});}
            var Q4;
            {var subQ0=sQuery(id+"F28.wireOp",EDGE,"E67");var subQ1=makeQuery(id+"F27.opExtrude","SWEPT_EDGE",EDGE,{"disambiguationData":[OSD([sQuery(id+"F11.wireOp",EDGE,"E32.top"),sQuery(id+"F11.wireOp",EDGE,"E32.right")])]});var subQ2=makeQuery(id+"F28.imprint","INTERSECT",VERTEX,{"disambiguationData":[OD(0.0)],"derivedFrom":[subQ1,subQ0]});Q4=makeQuery(id+"F28.imprint","IMPRINT",FACE,{"disambiguationData":[TD([[makeQuery(id+"F28.imprint","IMPRINT",EDGE,{"disambiguationData":[TD([[subQ2,-1.0]])],"derivedFrom":subQ0}),1.0]])]});}
            var Q5;
            {var subQ0=sQuery(id+"F28.wireOp",EDGE,"E67");var subQ1=sQuery(id+"F11.wireOp",EDGE,"E32.right");var subQ2=makeQuery(id+"F27.opExtrude","SWEPT_EDGE",EDGE,{"disambiguationData":[OSD([sQuery(id+"F11.wireOp",EDGE,"E32.top"),subQ1])]});var subQ3=makeQuery(id+"F28.imprint","INTERSECT",VERTEX,{"disambiguationData":[OD(0.0)],"derivedFrom":[subQ2,subQ0]});Q5=makeQuery(id+"F28.imprint","IMPRINT",FACE,{"disambiguationData":[TD([[makeQuery(id+"F28.imprint","IMPRINT",EDGE,{"disambiguationData":[TD([[subQ3,1.0]])],"derivedFrom":subQ0}),1.0]])]});}
            var Q6;
            {var subQ0=sQuery(id+"F28.wireOp",EDGE,"E67");var subQ1=makeQuery(id+"F27.opExtrude","SWEPT_EDGE",EDGE,{"disambiguationData":[OSD([sQuery(id+"F11.wireOp",EDGE,"E29.0"),sQuery(id+"F11.wireOp",EDGE,"E32.bottom"),sQuery(id+"F11.wireOp",EDGE,"E32.right")])]});var subQ2=makeQuery(id+"F28.imprint","INTERSECT",VERTEX,{"disambiguationData":[OD(0.0)],"derivedFrom":[subQ1,subQ0]});Q6=makeQuery(id+"F28.imprint","IMPRINT",FACE,{"disambiguationData":[TD([[makeQuery(id+"F28.imprint","IMPRINT",EDGE,{"disambiguationData":[TD([[subQ2,1.0]])],"derivedFrom":subQ0}),1.0]])]});}
            var Q7;
            Q7=makeQuery(id+"F27.opExtrude","SWEPT_FACE",FACE,{"disambiguationData":[OSD([sQuery(id+"F11.wireOp",EDGE,"E33.left")])]});
            extrude(context, id + "F29", {"entities" : qUnion([Q0, Q1, Q2, Q3, Q4, Q5, Q6]), "endBound" : BoundingType.UP_TO_SURFACE, "depth" : 25 * mm, "endBoundEntityFace" : qUnion([Q7]), "offsetDistance" : 25 * mm});
        }
        {
            var Q0;
            {var subQ7=sQuery(id+"F28.wireOp",EDGE,"E69");Q0=makeQuery(id+"F28.imprint","IMPRINT",FACE,{"disambiguationData":[TD([[makeQuery(id+"F28.imprint","IMPRINT",EDGE,{"derivedFrom":subQ7}),-1.0]])]});}
            var Q1;
            {var subQ0=sQuery(id+"F28.wireOp",EDGE,"E75.bottom");var subQ1=sQuery(id+"F28.wireOp",EDGE,"E70");var subQ2=makeQuery(id+"F28.imprint","INTERSECT",VERTEX,{"derivedFrom":[subQ1,subQ0]});Q1=makeQuery(id+"F28.imprint","IMPRINT",FACE,{"disambiguationData":[TD([[makeQuery(id+"F28.imprint","IMPRINT",EDGE,{"disambiguationData":[TD([[subQ2,-1.0]])],"derivedFrom":subQ1}),1.0]])]});}
            var Q2;
            {var subQ7=sQuery(id+"F28.wireOp",EDGE,"E70");var subQ8=sQuery(id+"F28.wireOp",EDGE,"E67");var subQ9=makeQuery(id+"F28.imprint","INTERSECT",VERTEX,{"derivedFrom":[subQ8,subQ7]});Q2=makeQuery(id+"F28.imprint","IMPRINT",FACE,{"disambiguationData":[TD([[makeQuery(id+"F28.imprint","IMPRINT",EDGE,{"disambiguationData":[TD([[subQ9,1.0]])],"derivedFrom":subQ7}),1.0]])]});}
            var Q3;
            {var subQ0=sQuery(id+"F28.wireOp",EDGE,"E67");var subQ1=sQuery(id+"F11.wireOp",EDGE,"E32.right");var subQ2=makeQuery(id+"F27.opExtrude","SWEPT_EDGE",EDGE,{"disambiguationData":[OSD([sQuery(id+"F11.wireOp",EDGE,"E32.top"),subQ1])]});var subQ3=makeQuery(id+"F28.imprint","INTERSECT",VERTEX,{"disambiguationData":[OD(1.0)],"derivedFrom":[subQ2,subQ0]});Q3=makeQuery(id+"F28.imprint","IMPRINT",FACE,{"disambiguationData":[TD([[makeQuery(id+"F28.imprint","IMPRINT",EDGE,{"disambiguationData":[TD([[subQ3,-1.0]])],"derivedFrom":subQ0}),-1.0]])]});}
            extrude(context, id + "F30", {"entities" : qUnion([Q0, Q1, Q2, Q3]), "depth" : 10 * mm, "offsetDistance" : 25 * mm});
        }
        {
            var Q0;
            {var subQ0=sQuery(id+"F28.wireOp",EDGE,"E75.bottom");var subQ1=sQuery(id+"F28.wireOp",EDGE,"E72.0");var subQ2=makeQuery(id+"F28.imprint","INTERSECT",VERTEX,{"derivedFrom":[subQ1,subQ0]});Q0=makeQuery(id+"F28.imprint","IMPRINT",FACE,{"disambiguationData":[TD([[makeQuery(id+"F28.imprint","IMPRINT",EDGE,{"disambiguationData":[TD([[subQ2,-1.0]])],"derivedFrom":subQ1}),1.0]])]});}
            var Q1;
            {var subQ5=sQuery(id+"F28.wireOp",EDGE,"E75.left");Q1=makeQuery(id+"F28.imprint","IMPRINT",FACE,{"disambiguationData":[TD([[makeQuery(id+"F28.imprint","IMPRINT",EDGE,{"derivedFrom":subQ5}),1.0]])]});}
            var Q2;
            {var subQ0=sQuery(id+"F28.wireOp",EDGE,"E75.bottom");var subQ1=sQuery(id+"F28.wireOp",EDGE,"E70");var subQ2=makeQuery(id+"F28.imprint","INTERSECT",VERTEX,{"derivedFrom":[subQ1,subQ0]});Q2=makeQuery(id+"F28.imprint","IMPRINT",FACE,{"disambiguationData":[TD([[makeQuery(id+"F28.imprint","IMPRINT",EDGE,{"disambiguationData":[TD([[subQ2,-1.0]])],"derivedFrom":subQ1}),1.0]])]});}
            var Q3;
            {var subQ3=sQuery(id+"F28.wireOp",EDGE,"E78.bottom");Q3=makeQuery(id+"F28.imprint","IMPRINT",FACE,{"disambiguationData":[TD([[makeQuery(id+"F28.imprint","IMPRINT",EDGE,{"derivedFrom":subQ3}),-1.0]])]});}
            extrude(context, id + "F31", {"entities" : qUnion([Q0, Q1, Q2, Q3]), "operationType" : NewBodyOperationType.ADD, "depth" : 20 * mm, "offsetDistance" : 25 * mm});
        }
    });
